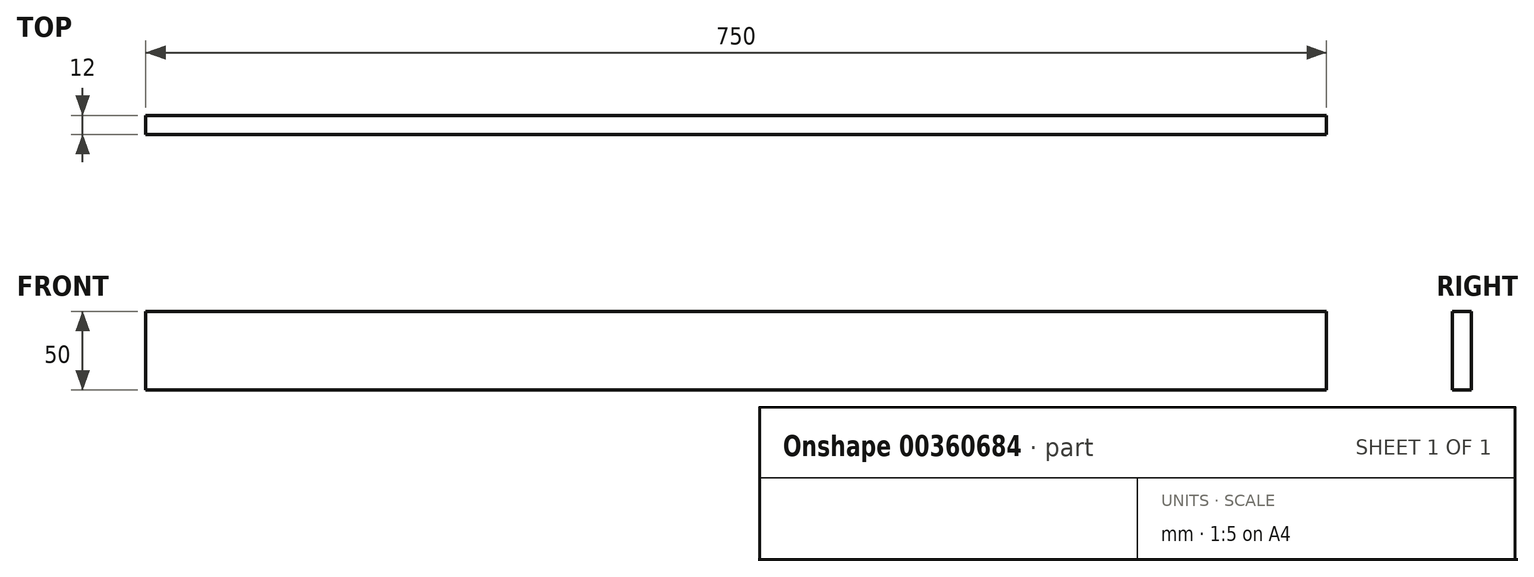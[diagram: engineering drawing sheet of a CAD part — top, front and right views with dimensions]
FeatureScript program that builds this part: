
annotation { "Feature Type Name" : "Feature", "Feature Type Description" : "" }
export const myFeature = defineFeature(function(context is Context, id is Id, definition is map)
    precondition{}
    {
        {
            var Q0;
            Q0=qCreatedBy(makeId("Front.planeOp"),FACE);
            var sketch = newSketch(context, id + "F0", { "sketchPlane" : qUnion([Q0])});
            skLineSegment(sketch, "E0.bottom", {"start": v(0, 0) * mm, "end": v(750, 0) * mm});
            skLineSegment(sketch, "E0.top", {"start": v(0, 50) * mm, "end": v(750, 50) * mm});
            skLineSegment(sketch, "E0.left", {"start": v(0, 0) * mm, "end": v(0, 50) * mm});
            skLineSegment(sketch, "E0.right", {"start": v(750, 0) * mm, "end": v(750, 50) * mm});
            skSolve(sketch);
        }
        {
            var Q0;
            Q0=makeQuery(id+"F0.imprint","IMPRINT",FACE,{"disambiguationData":[TD([[makeQuery(id+"F0.imprint","IMPRINT",EDGE,{"derivedFrom":sQuery(id+"F0.wireOp",EDGE,"ESCJjQW9-Kipg-MWqb-1C1w-8BTgatxLSc3F.bottom")}),1.0]])]});
            var Q1;
            Q1=makeQuery(id+"F0.imprint","IMPRINT",FACE,{"disambiguationData":[TD([[makeQuery(id+"F0.imprint","IMPRINT",EDGE,{"derivedFrom":sQuery(id+"F0.wireOp",EDGE,"E0.bottom")}),1.0]])]});
            extrude(context, id + "F1", {"entities" : qUnion([Q0, Q1]), "depth" : 12 * mm});
        }
    });
